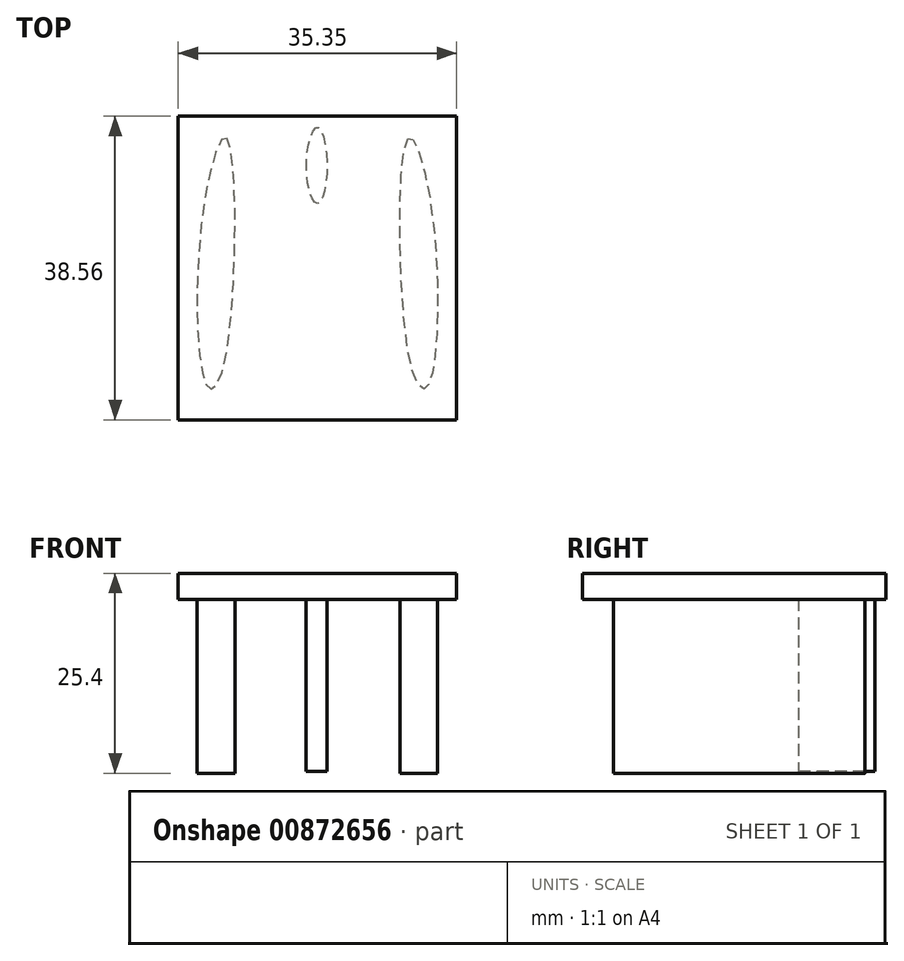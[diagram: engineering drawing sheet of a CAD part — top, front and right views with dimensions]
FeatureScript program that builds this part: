
annotation { "Feature Type Name" : "Feature", "Feature Type Description" : "" }
export const myFeature = defineFeature(function(context is Context, id is Id, definition is map)
    precondition{}
    {
        {
            var Q0;
            Q0=qCreatedBy(makeId("Top.planeOp"),FACE);
            var sketch = newSketch(context, id + "F0", { "sketchPlane" : qUnion([Q0])});
            skFitSpline(sketch, "E0", {"points": [v(-31.08, 25.25) * mm, v(-33.54, 19.57) * mm, v(-34.62, -1.77) * mm, v(-33.23, -6.52) * mm, v(-31.24, -2.53) * mm, v(-31.08, 25.25) * mm]});
            skSolve(sketch);
        }
        {
            var Q0;
            Q0=makeQuery(id+"F0.imprint","IMPRINT",FACE,{"disambiguationData":[TD([[makeQuery(id+"F0.imprint","IMPRINT",EDGE,{"derivedFrom":sQuery(id+"F0.wireOp",EDGE,"E0")}),1.0]])]});
            extrude(context, id + "F1", {"entities" : qUnion([Q0]), "depth" : 25.4 * mm, "offsetDistance" : 25.4 * mm});
        }
        {
            var Q0;
            Q0=makeQuery(id+"F1.opExtrude","CAP_FACE",FACE,{"disambiguationData":[OSD([sQuery(id+"F0.wireOp",EDGE,"E0")])],"isStart":false});
            var sketch = newSketch(context, id + "F2", { "sketchPlane" : qUnion([Q0])});
            skLineSegment(sketch, "E1.bottom", {"start": v(-37.28, -10.49) * mm, "end": v(-19.6, -10.49) * mm});
            skLineSegment(sketch, "E1.top", {"start": v(-37.28, 28.07) * mm, "end": v(-19.6, 28.07) * mm});
            skLineSegment(sketch, "E1.left", {"start": v(-37.28, -10.49) * mm, "end": v(-37.28, 28.07) * mm});
            skLineSegment(sketch, "E1.right", {"start": v(-19.6, -10.49) * mm, "end": v(-19.6, 28.07) * mm});
            skSolve(sketch);
        }
        {
            var Q0;
            Q0=makeQuery(id+"F2.imprint","IMPRINT",FACE,{"disambiguationData":[TD([[makeQuery(id+"F2.imprint","IMPRINT",EDGE,{"derivedFrom":sQuery(id+"F2.wireOp",EDGE,"E1.bottom")}),1.0]])]});
            extrude(context, id + "F3", {"entities" : qUnion([Q0]), "operationType" : NewBodyOperationType.ADD, "oppositeDirection" : true, "depth" : 3.3 * mm, "offsetDistance" : 25.4 * mm});
        }
        {
            var Q0;
            Q0=makeQuery(id+"F1.opExtrude","SWEPT_BODY",BODY,{"disambiguationData":[OSD([sQuery(id+"F0.wireOp",EDGE,"E0")])]});
            var Q1;
            Q1=makeQuery(id+"F3.opExtrude","SWEPT_FACE",FACE,{"disambiguationData":[OSD([sQuery(id+"F2.wireOp",EDGE,"E1.right")])]});
            mirror(context, id + "F4", {"operationType" : NewBodyOperationType.ADD, "entities" : qUnion([Q0]), "mirrorPlane" : qUnion([Q1])});
        }
        {
            var Q0;
            {var subQ0=makeQuery(id+"F3.opExtrude","CAP_FACE",FACE,{"disambiguationData":[OSD([sQuery(id+"F0.wireOp",EDGE,"E0"),sQuery(id+"F2.wireOp",EDGE,"E1.bottom"),sQuery(id+"F2.wireOp",EDGE,"E1.top"),sQuery(id+"F2.wireOp",EDGE,"E1.left"),sQuery(id+"F2.wireOp",EDGE,"E1.right")])],"isStart":false});Q0=makeQuery(id+"F4.boolean.opBoolean","MERGE",FACE,{"derivedFrom":[subQ0,makeQuery(id+"F4.opPattern","COPY",FACE,{"derivedFrom":subQ0,"instanceName":"1"})]});}
            var sketch = newSketch(context, id + "F5", { "sketchPlane" : qUnion([Q0])});
            skPoint(sketch, "E2.0.internal.snap0", {"position": v(-19.6, 10.49) * mm});
            skPoint(sketch, "E2.2.internal.snap0", {"position": v(-19.6, 10.49) * mm});
            skFitSpline(sketch, "E2", {"points": [v(-19.6, -16.96) * mm, v(-21.01, -21.52) * mm, v(-19.6, -26.68) * mm, v(-18.36, -21.54) * mm, v(-19.6, -16.96) * mm]});
            skSolve(sketch);
        }
        {
            var Q0;
            Q0=makeQuery(id+"F5.imprint","IMPRINT",FACE,{"disambiguationData":[TD([[makeQuery(id+"F5.imprint","IMPRINT",EDGE,{"derivedFrom":sQuery(id+"F5.wireOp",EDGE,"E2")}),1.0]])]});
            extrude(context, id + "F6", {"entities" : qUnion([Q0]), "operationType" : NewBodyOperationType.ADD, "depth" : 19.05 * mm, "offsetDistance" : 25.4 * mm});
        }
        {
            var Q0;
            Q0 = qSketchRegion(id + "F5", true);
            extrude(context, id + "F7", {"entities" : qUnion([Q0]), "operationType" : NewBodyOperationType.ADD, "depth" : 21.84 * mm, "offsetDistance" : 25.4 * mm});
        }
    });
